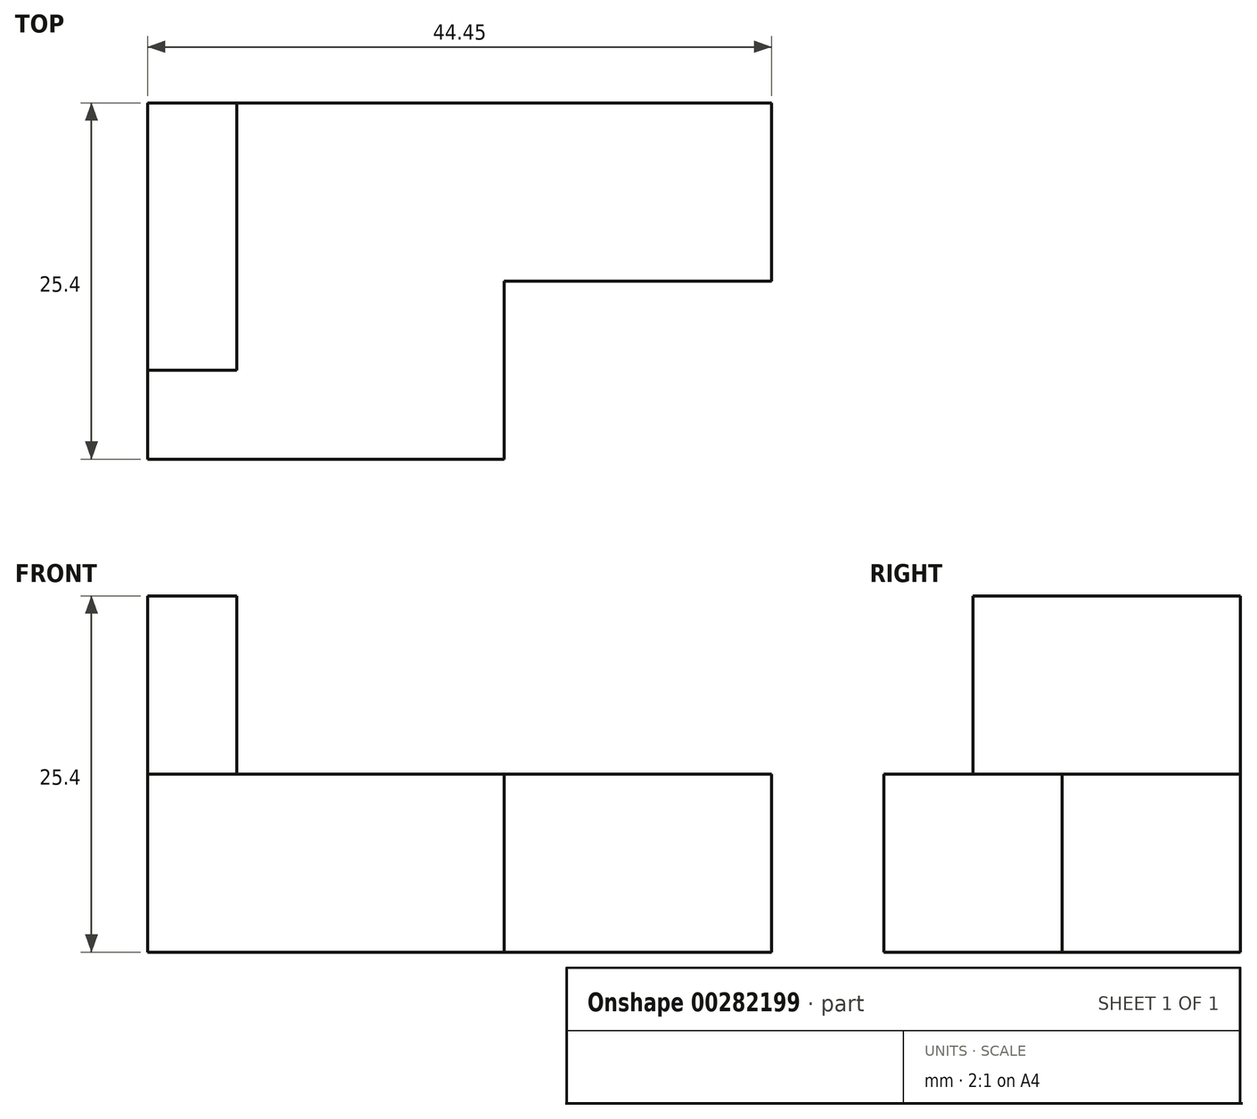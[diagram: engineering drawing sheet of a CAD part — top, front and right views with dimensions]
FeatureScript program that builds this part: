
annotation { "Feature Type Name" : "Feature", "Feature Type Description" : "" }
export const myFeature = defineFeature(function(context is Context, id is Id, definition is map)
    precondition{}
    {
        {
            var Q0;
            Q0=qCreatedBy(makeId("Top.planeOp"),FACE);
            var sketch = newSketch(context, id + "F0", { "sketchPlane" : qUnion([Q0])});
            skLineSegment(sketch, "E0.bottom", {"start": v(0, 0) * mm, "end": v(25.4, 0) * mm});
            skLineSegment(sketch, "E0.top", {"start": v(0, -25.4) * mm, "end": v(25.4, -25.4) * mm});
            skLineSegment(sketch, "E0.left", {"start": v(0, 0) * mm, "end": v(0, -25.4) * mm});
            skLineSegment(sketch, "E0.right", {"start": v(25.4, 0) * mm, "end": v(25.4, -25.4) * mm});
            skSolve(sketch);
        }
        {
            var Q0;
            Q0 = qSketchRegion(id + "F0", true);
            extrude(context, id + "F1", {"entities" : qUnion([Q0]), "depth" : 12.7 * mm});
        }
        {
            var Q0;
            Q0=makeQuery(id+"F1.opExtrude","CAP_FACE",FACE,{"disambiguationData":[OSD([sQuery(id+"F0.wireOp",EDGE,"E0.bottom"),sQuery(id+"F0.wireOp",EDGE,"E0.top"),sQuery(id+"F0.wireOp",EDGE,"E0.left"),sQuery(id+"F0.wireOp",EDGE,"E0.right")])],"isStart":false});
            var sketch = newSketch(context, id + "F2", { "sketchPlane" : qUnion([Q0])});
            skLineSegment(sketch, "E1.bottom", {"start": v(0, 0) * mm, "end": v(6.35, 0) * mm});
            skLineSegment(sketch, "E1.top", {"start": v(0, -19.05) * mm, "end": v(6.35, -19.05) * mm});
            skLineSegment(sketch, "E1.left", {"start": v(0, 0) * mm, "end": v(0, -19.05) * mm});
            skLineSegment(sketch, "E1.right", {"start": v(6.35, 0) * mm, "end": v(6.35, -19.05) * mm});
            skSolve(sketch);
        }
        {
            var Q0;
            Q0 = qSketchRegion(id + "F2", true);
            extrude(context, id + "F3", {"entities" : qUnion([Q0]), "operationType" : NewBodyOperationType.ADD, "depth" : 12.7 * mm});
        }
        {
            var Q0;
            Q0=makeQuery(id+"F1.opExtrude","SWEPT_FACE",FACE,{"disambiguationData":[OSD([sQuery(id+"F0.wireOp",EDGE,"E0.right")])]});
            var sketch = newSketch(context, id + "F4", { "sketchPlane" : qUnion([Q0])});
            skLineSegment(sketch, "E2.bottom", {"start": v(0, 12.7) * mm, "end": v(-12.7, 12.7) * mm});
            skLineSegment(sketch, "E2.top", {"start": v(0, 0) * mm, "end": v(-12.7, 0) * mm});
            skLineSegment(sketch, "E2.left", {"start": v(0, 12.7) * mm, "end": v(0, 0) * mm});
            skLineSegment(sketch, "E2.right", {"start": v(-12.7, 12.7) * mm, "end": v(-12.7, 0) * mm});
            skSolve(sketch);
        }
        {
            var Q0;
            Q0 = qSketchRegion(id + "F4", true);
            extrude(context, id + "F5", {"entities" : qUnion([Q0]), "operationType" : NewBodyOperationType.ADD, "depth" : 19.05 * mm});
        }
    });
